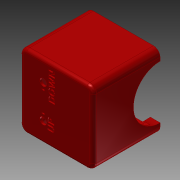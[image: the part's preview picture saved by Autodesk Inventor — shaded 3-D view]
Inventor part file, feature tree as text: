
AUTODESK INVENTOR PART (.ipt)
format: ipt  version: 2015 (Build 190159000, 159)  size: 355,840 bytes
history: native  units: in
note: dims shown in document units (in); Inventor stores cm internally (conversion verified against a paired STEP export)
features: extrude x5, sketch x5, shell x1, fillet x1
ambient origin geometry x8: Origin, YZ Plane, XZ Plane, XY Plane, X Axis, Y Axis, Z Axis, Center Point
bodies: Solid1 (feature_tree)
feature tree (12):
  extrude  "Extrusion1"  Depth=2.75in
  shell  "Shell1"  Thickness=0.25in
  extrude  "Extrusion2"  Depth=0.17in
  fillet  "Fillet2"  Radius=0.17in
  extrude  "Extrusion3"  Depth=1.0in TaperAngle=0.0deg
  extrude  "Extrusion4"  Depth=0.125in
  extrude  "Extrusion5"  Depth=1.0in
  sketch  "Sketch1"  dims[d0=2.75in d1=2.75in d2=0.25in]
  sketch  "Sketch4"  dims[d3=2.5in d4=0.0in d5=0.08in d7=0.17in]
  sketch  "Sketch5"  dims[d8=0.17in d9=1.0in d10=0.0in]
  sketch  "Sketch6"  dims[d11=0.1142in d12=0.125in]
  sketch  "Sketch7"  dims[d31=0.24in d32=0.27in d33=0.1in d34=0.05in d35=1.25in d36=0.5in d37=1.0in d38=0.0in d39=0.125in d40=0.125in d41=0.2033in d42=0.4975in d43=0.05in d44=0.0in d45=1.0in d46=1.0in d47=0.0in]
